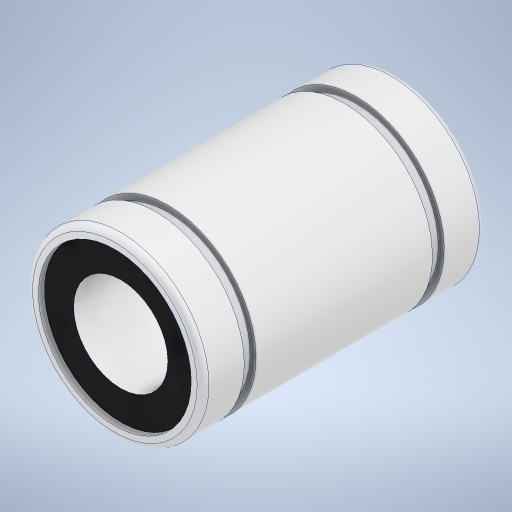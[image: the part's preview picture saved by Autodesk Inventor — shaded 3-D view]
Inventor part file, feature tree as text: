
AUTODESK INVENTOR PART (.ipt)
format: ipt  version: 2023 (Build 270158000, 158)  size: 317,952 bytes
history: native  units: mm
features: extrude x3, sketch x3, fillet x1, revolve x1, projected_geometry x1
ambient origin geometry x8: Origin, YZ Plane, XZ Plane, XY Plane, X Axis, Y Axis, Z Axis, Center Point
bodies: Solid1 (feature_tree)
feature tree (9):
  extrude  "Extrusion1"  Depth=15.0mm
  fillet  "Fillet1"  Radius=15.0mm
  revolve  "Revolution1"  [1 undecoded]
  sketch  "Sketch3"  dims[d6=1.0mm d7=0.5mm d8=90.0deg d9=1.0mm d10=0.5mm d11=0.0mm d12=0.5mm d13=0.0mm]
  extrude  "Extrusion2"  Depth=0.5mm
  extrude  "Extrusion3"  TaperAngle=90.0deg  [1 undecoded]
  sketch  "Sketch1"  dims[d0=24.0mm d1=0.0mm d2=8.0mm d3=15.0mm]
  sketch  "Sketch2"  dims[d4=0.5mm d5=3.5mm]
  projected_geometry  "Project Cut Edges1"
note: 2 required parameter values undecoded (feature->parameter linkage not recoverable at this tier; creation-order binding heuristic only, values carry confidence <= 0.55)